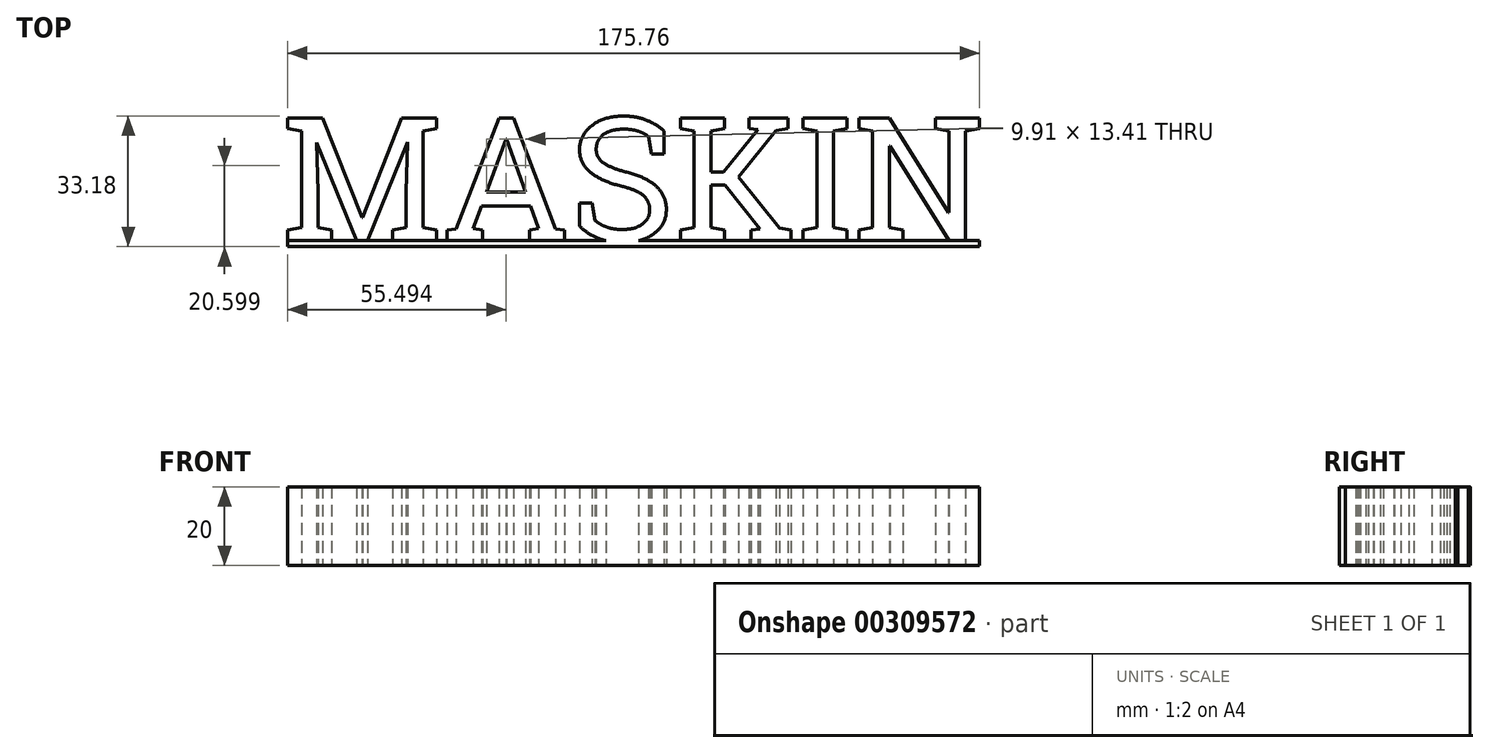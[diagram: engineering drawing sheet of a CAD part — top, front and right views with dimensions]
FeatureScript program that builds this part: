
annotation { "Feature Type Name" : "Feature", "Feature Type Description" : "" }
export const myFeature = defineFeature(function(context is Context, id is Id, definition is map)
    precondition{}
    {
        {
            var Q0;
            Q0=qCreatedBy(makeId("Top.planeOp"),FACE);
            var sketch = newSketch(context, id + "F0", { "sketchPlane" : qUnion([Q0])});
            skText(sketch, "E0", { "text": "MASKIN", "fontName": "RobotoSlab-Regular.ttf"});
            skLineSegment(sketch, "E1.bottom", {"start": v(-307.65, 25.18) * mm, "end": v(-127.65, 25.18) * mm});
            skLineSegment(sketch, "E1.top", {"start": v(-307.65, 23.68) * mm, "end": v(-127.65, 23.68) * mm});
            skLineSegment(sketch, "E1.left", {"start": v(-307.65, 25.18) * mm, "end": v(-307.65, 23.68) * mm});
            skLineSegment(sketch, "E1.right", {"start": v(-127.65, 25.18) * mm, "end": v(-127.65, 23.68) * mm});
            const initialGuessF0  = {"E0": [-0.30765, 0.02518, 1, 0, 0.03163]};
            skSetInitialGuess(sketch, initialGuessF0);
            skSolve(sketch);
        }
        {
            var Q0;
            Q0 = qSketchRegion(id + "F0", true);
            extrude(context, id + "F1", {"entities" : qUnion([Q0]), "depth" : 20 * mm, "offsetDistance" : 25 * mm});
        }
        {
            var Q0;
            Q0=makeQuery(id+"F1.opExtrude","CAP_FACE",FACE,{"disambiguationData":[OSD([sQuery(id+"F0.wireOp",EDGE,"E0.sketch_text.stroke-0"),sQuery(id+"F0.wireOp",EDGE,"E0.sketch_text.stroke-1"),sQuery(id+"F0.wireOp",EDGE,"E0.sketch_text.stroke-3"),sQuery(id+"F0.wireOp",EDGE,"E0.sketch_text.stroke-4"),sQuery(id+"F0.wireOp",EDGE,"E0.sketch_text.stroke-5"),sQuery(id+"F0.wireOp",EDGE,"E0.sketch_text.stroke-6"),sQuery(id+"F0.wireOp",EDGE,"E0.sketch_text.stroke-7"),sQuery(id+"F0.wireOp",EDGE,"E0.sketch_text.stroke-8"),sQuery(id+"F0.wireOp",EDGE,"E0.sketch_text.stroke-10"),sQuery(id+"F0.wireOp",EDGE,"E0.sketch_text.stroke-11"),sQuery(id+"F0.wireOp",EDGE,"E0.sketch_text.stroke-12"),sQuery(id+"F0.wireOp",EDGE,"E0.sketch_text.stroke-13"),sQuery(id+"F0.wireOp",EDGE,"E0.sketch_text.stroke-14"),sQuery(id+"F0.wireOp",EDGE,"E0.sketch_text.stroke-15"),sQuery(id+"F0.wireOp",EDGE,"E0.sketch_text.stroke-16"),sQuery(id+"F0.wireOp",EDGE,"E0.sketch_text.stroke-17"),sQuery(id+"F0.wireOp",EDGE,"E0.sketch_text.stroke-18"),sQuery(id+"F0.wireOp",EDGE,"E0.sketch_text.stroke-19"),sQuery(id+"F0.wireOp",EDGE,"E0.sketch_text.stroke-20"),sQuery(id+"F0.wireOp",EDGE,"E0.sketch_text.stroke-21"),sQuery(id+"F0.wireOp",EDGE,"E0.sketch_text.stroke-22"),sQuery(id+"F0.wireOp",EDGE,"E0.sketch_text.stroke-23"),sQuery(id+"F0.wireOp",EDGE,"E0.sketch_text.stroke-24"),sQuery(id+"F0.wireOp",EDGE,"E0.sketch_text.stroke-25"),sQuery(id+"F0.wireOp",EDGE,"E0.sketch_text.stroke-27"),sQuery(id+"F0.wireOp",EDGE,"E0.sketch_text.stroke-28"),sQuery(id+"F0.wireOp",EDGE,"E0.sketch_text.stroke-29"),sQuery(id+"F0.wireOp",EDGE,"E0.sketch_text.stroke-30"),sQuery(id+"F0.wireOp",EDGE,"E0.sketch_text.stroke-31"),sQuery(id+"F0.wireOp",EDGE,"E0.sketch_text.stroke-32"),sQuery(id+"F0.wireOp",EDGE,"E0.sketch_text.stroke-33"),sQuery(id+"F0.wireOp",EDGE,"E0.sketch_text.stroke-34"),sQuery(id+"F0.wireOp",EDGE,"E0.sketch_text.stroke-35"),sQuery(id+"F0.wireOp",EDGE,"E0.sketch_text.stroke-36"),sQuery(id+"F0.wireOp",EDGE,"E0.sketch_text.stroke-38"),sQuery(id+"F0.wireOp",EDGE,"E0.sketch_text.stroke-39"),sQuery(id+"F0.wireOp",EDGE,"E0.sketch_text.stroke-40"),sQuery(id+"F0.wireOp",EDGE,"E0.sketch_text.stroke-41"),sQuery(id+"F0.wireOp",EDGE,"E0.sketch_text.stroke-42"),sQuery(id+"F0.wireOp",EDGE,"E0.sketch_text.stroke-43"),sQuery(id+"F0.wireOp",EDGE,"E0.sketch_text.stroke-44"),sQuery(id+"F0.wireOp",EDGE,"E0.sketch_text.stroke-46"),sQuery(id+"F0.wireOp",EDGE,"E0.sketch_text.stroke-47"),sQuery(id+"F0.wireOp",EDGE,"E0.sketch_text.stroke-48"),sQuery(id+"F0.wireOp",EDGE,"E0.sketch_text.stroke-49"),sQuery(id+"F0.wireOp",EDGE,"E0.sketch_text.stroke-50"),sQuery(id+"F0.wireOp",EDGE,"E0.sketch_text.stroke-51"),sQuery(id+"F0.wireOp",EDGE,"E0.sketch_text.stroke-52"),sQuery(id+"F0.wireOp",EDGE,"E0.sketch_text.stroke-53"),sQuery(id+"F0.wireOp",EDGE,"E0.sketch_text.stroke-54"),sQuery(id+"F0.wireOp",EDGE,"E0.sketch_text.stroke-55"),sQuery(id+"F0.wireOp",EDGE,"E0.sketch_text.stroke-56"),sQuery(id+"F0.wireOp",EDGE,"E0.sketch_text.stroke-57"),sQuery(id+"F0.wireOp",EDGE,"E0.sketch_text.stroke-58"),sQuery(id+"F0.wireOp",EDGE,"E0.sketch_text.stroke-59"),sQuery(id+"F0.wireOp",EDGE,"E0.sketch_text.stroke-60"),sQuery(id+"F0.wireOp",EDGE,"E0.sketch_text.stroke-61"),sQuery(id+"F0.wireOp",EDGE,"E0.sketch_text.stroke-62"),sQuery(id+"F0.wireOp",EDGE,"E0.sketch_text.stroke-63"),sQuery(id+"F0.wireOp",EDGE,"E0.sketch_text.stroke-64"),sQuery(id+"F0.wireOp",EDGE,"E0.sketch_text.stroke-65"),sQuery(id+"F0.wireOp",EDGE,"E0.sketch_text.stroke-66"),sQuery(id+"F0.wireOp",EDGE,"E0.sketch_text.stroke-67"),sQuery(id+"F0.wireOp",EDGE,"E0.sketch_text.stroke-68"),sQuery(id+"F0.wireOp",EDGE,"E0.sketch_text.stroke-69"),sQuery(id+"F0.wireOp",EDGE,"E0.sketch_text.stroke-70"),sQuery(id+"F0.wireOp",EDGE,"E0.sketch_text.stroke-71"),sQuery(id+"F0.wireOp",EDGE,"E0.sketch_text.stroke-72"),sQuery(id+"F0.wireOp",EDGE,"E0.sketch_text.stroke-73"),sQuery(id+"F0.wireOp",EDGE,"E0.sketch_text.stroke-74"),sQuery(id+"F0.wireOp",EDGE,"E0.sketch_text.stroke-75"),sQuery(id+"F0.wireOp",EDGE,"E0.sketch_text.stroke-76"),sQuery(id+"F0.wireOp",EDGE,"E0.sketch_text.stroke-77"),sQuery(id+"F0.wireOp",EDGE,"E0.sketch_text.stroke-78"),sQuery(id+"F0.wireOp",EDGE,"E0.sketch_text.stroke-79"),sQuery(id+"F0.wireOp",EDGE,"E0.sketch_text.stroke-80"),sQuery(id+"F0.wireOp",EDGE,"E0.sketch_text.stroke-81"),sQuery(id+"F0.wireOp",EDGE,"E0.sketch_text.stroke-82"),sQuery(id+"F0.wireOp",EDGE,"E0.sketch_text.stroke-83"),sQuery(id+"F0.wireOp",EDGE,"E0.sketch_text.stroke-84"),sQuery(id+"F0.wireOp",EDGE,"E0.sketch_text.stroke-85"),sQuery(id+"F0.wireOp",EDGE,"E0.sketch_text.stroke-86"),sQuery(id+"F0.wireOp",EDGE,"E0.sketch_text.stroke-87"),sQuery(id+"F0.wireOp",EDGE,"E0.sketch_text.stroke-88"),sQuery(id+"F0.wireOp",EDGE,"E0.sketch_text.stroke-89"),sQuery(id+"F0.wireOp",EDGE,"E0.sketch_text.stroke-90"),sQuery(id+"F0.wireOp",EDGE,"E0.sketch_text.stroke-91"),sQuery(id+"F0.wireOp",EDGE,"E0.sketch_text.stroke-92"),sQuery(id+"F0.wireOp",EDGE,"E0.sketch_text.stroke-93"),sQuery(id+"F0.wireOp",EDGE,"E0.sketch_text.stroke-94"),sQuery(id+"F0.wireOp",EDGE,"E0.sketch_text.stroke-95"),sQuery(id+"F0.wireOp",EDGE,"E0.sketch_text.stroke-96"),sQuery(id+"F0.wireOp",EDGE,"E0.sketch_text.stroke-97"),sQuery(id+"F0.wireOp",EDGE,"E0.sketch_text.stroke-98"),sQuery(id+"F0.wireOp",EDGE,"E0.sketch_text.stroke-99"),sQuery(id+"F0.wireOp",EDGE,"E0.sketch_text.stroke-101"),sQuery(id+"F0.wireOp",EDGE,"E0.sketch_text.stroke-102"),sQuery(id+"F0.wireOp",EDGE,"E0.sketch_text.stroke-103"),sQuery(id+"F0.wireOp",EDGE,"E0.sketch_text.stroke-104"),sQuery(id+"F0.wireOp",EDGE,"E0.sketch_text.stroke-105"),sQuery(id+"F0.wireOp",EDGE,"E0.sketch_text.stroke-106"),sQuery(id+"F0.wireOp",EDGE,"E0.sketch_text.stroke-107"),sQuery(id+"F0.wireOp",EDGE,"E0.sketch_text.stroke-109"),sQuery(id+"F0.wireOp",EDGE,"E0.sketch_text.stroke-110"),sQuery(id+"F0.wireOp",EDGE,"E0.sketch_text.stroke-111"),sQuery(id+"F0.wireOp",EDGE,"E0.sketch_text.stroke-112"),sQuery(id+"F0.wireOp",EDGE,"E0.sketch_text.stroke-113"),sQuery(id+"F0.wireOp",EDGE,"E0.sketch_text.stroke-114"),sQuery(id+"F0.wireOp",EDGE,"E0.sketch_text.stroke-115"),sQuery(id+"F0.wireOp",EDGE,"E0.sketch_text.stroke-116"),sQuery(id+"F0.wireOp",EDGE,"E0.sketch_text.stroke-118"),sQuery(id+"F0.wireOp",EDGE,"E0.sketch_text.stroke-119"),sQuery(id+"F0.wireOp",EDGE,"E0.sketch_text.stroke-120"),sQuery(id+"F0.wireOp",EDGE,"E0.sketch_text.stroke-121"),sQuery(id+"F0.wireOp",EDGE,"E0.sketch_text.stroke-122"),sQuery(id+"F0.wireOp",EDGE,"E0.sketch_text.stroke-123"),sQuery(id+"F0.wireOp",EDGE,"E0.sketch_text.stroke-124"),sQuery(id+"F0.wireOp",EDGE,"E0.sketch_text.stroke-126"),sQuery(id+"F0.wireOp",EDGE,"E0.sketch_text.stroke-127"),sQuery(id+"F0.wireOp",EDGE,"E0.sketch_text.stroke-128"),sQuery(id+"F0.wireOp",EDGE,"E0.sketch_text.stroke-129"),sQuery(id+"F0.wireOp",EDGE,"E0.sketch_text.stroke-130"),sQuery(id+"F0.wireOp",EDGE,"E0.sketch_text.stroke-132"),sQuery(id+"F0.wireOp",EDGE,"E0.sketch_text.stroke-133"),sQuery(id+"F0.wireOp",EDGE,"E0.sketch_text.stroke-134"),sQuery(id+"F0.wireOp",EDGE,"E0.sketch_text.stroke-135"),sQuery(id+"F0.wireOp",EDGE,"E0.sketch_text.stroke-136"),sQuery(id+"F0.wireOp",EDGE,"E0.sketch_text.stroke-137"),sQuery(id+"F0.wireOp",EDGE,"E0.sketch_text.stroke-138"),sQuery(id+"F0.wireOp",EDGE,"E0.sketch_text.stroke-139"),sQuery(id+"F0.wireOp",EDGE,"E0.sketch_text.stroke-140"),sQuery(id+"F0.wireOp",EDGE,"E0.sketch_text.stroke-141"),sQuery(id+"F0.wireOp",EDGE,"E0.sketch_text.stroke-142"),sQuery(id+"F0.wireOp",EDGE,"E0.sketch_text.stroke-143"),sQuery(id+"F0.wireOp",EDGE,"E0.sketch_text.stroke-144"),sQuery(id+"F0.wireOp",EDGE,"E0.sketch_text.stroke-145"),sQuery(id+"F0.wireOp",EDGE,"E1.bottom"),sQuery(id+"F0.wireOp",EDGE,"E1.top"),sQuery(id+"F0.wireOp",EDGE,"E1.left"),sQuery(id+"F0.wireOp",EDGE,"E1.right")])],"isStart":false});
            var sketch = newSketch(context, id + "F2", { "sketchPlane" : qUnion([Q0])});
            skLineSegment(sketch, "E2.bottom", {"start": v(-306.12, 25.18) * mm, "end": v(-307.65, 25.18) * mm});
            skLineSegment(sketch, "E2.top", {"start": v(-306.12, 23.68) * mm, "end": v(-307.65, 23.68) * mm});
            skLineSegment(sketch, "E2.left", {"start": v(-306.12, 25.18) * mm, "end": v(-306.12, 23.68) * mm});
            skLineSegment(sketch, "E2.right", {"start": v(-307.65, 25.18) * mm, "end": v(-307.65, 23.68) * mm});
            skLineSegment(sketch, "E3.right", {"start": v(-127.65, 25.18) * mm, "end": v(-127.65, 23.68) * mm});
            skLineSegment(sketch, "E4.bottom", {"start": v(-130.37, 25.18) * mm, "end": v(-127.65, 25.18) * mm});
            skLineSegment(sketch, "E4.top", {"start": v(-130.37, 23.68) * mm, "end": v(-127.65, 23.68) * mm});
            skLineSegment(sketch, "E4.left", {"start": v(-130.37, 25.18) * mm, "end": v(-130.37, 23.68) * mm});
            skSolve(sketch);
        }
        {
            var Q0;
            Q0=makeQuery(id+"F2.imprint","IMPRINT",FACE,{"disambiguationData":[TD([[makeQuery(id+"F2.imprint","IMPRINT",EDGE,{"derivedFrom":sQuery(id+"F2.wireOp",EDGE,"E2.bottom")}),-1.0]])]});
            var Q1;
            Q1=makeQuery(id+"F2.imprint","IMPRINT",FACE,{"disambiguationData":[TD([[makeQuery(id+"F2.imprint","IMPRINT",EDGE,{"derivedFrom":sQuery(id+"F2.wireOp",EDGE,"E4.bottom")}),-1.0]])]});
            extrude(context, id + "F3", {"entities" : qUnion([Q0, Q1]), "operationType" : NewBodyOperationType.REMOVE, "endBound" : BoundingType.THROUGH_ALL, "oppositeDirection" : true, "depth" : 25 * mm, "offsetDistance" : 25 * mm});
        }
    });
